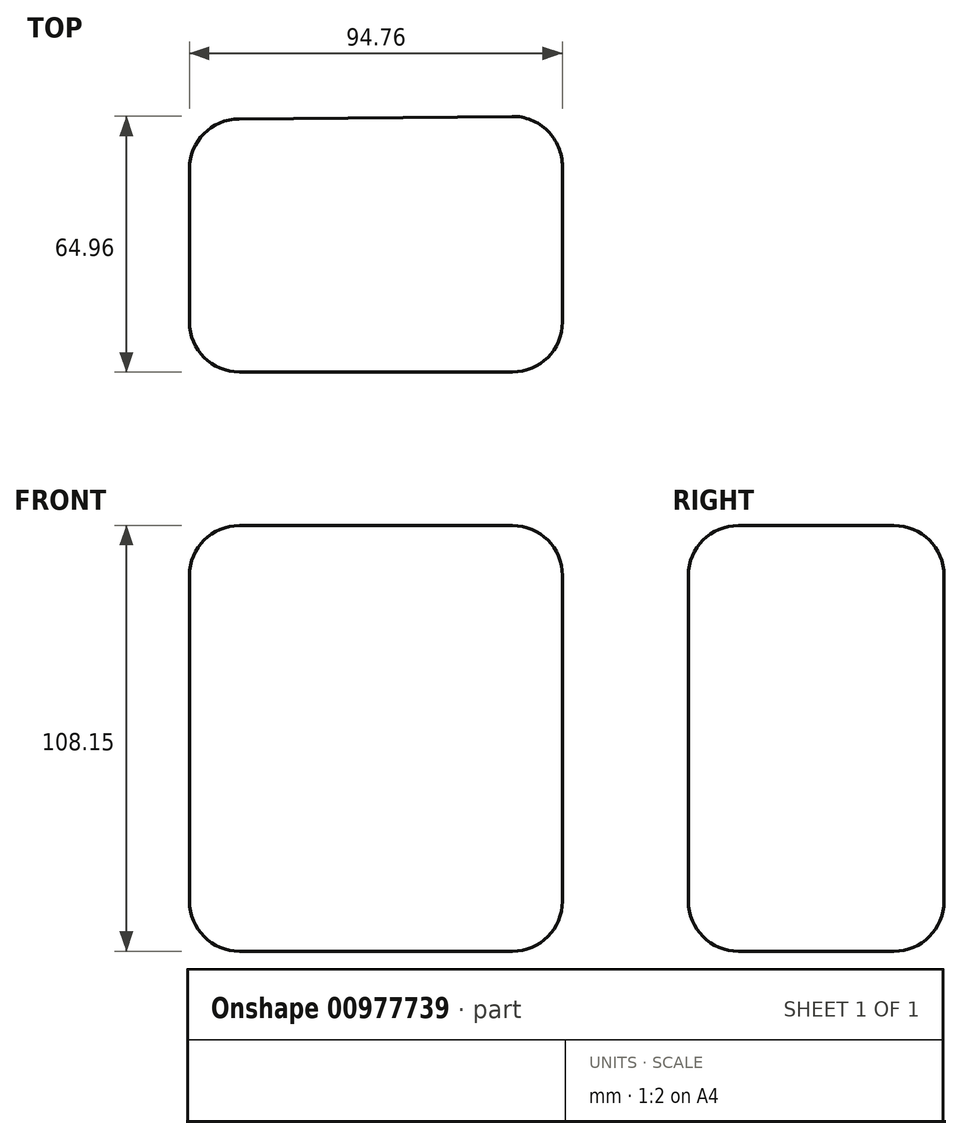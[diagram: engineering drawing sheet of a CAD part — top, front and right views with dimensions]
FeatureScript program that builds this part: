
annotation { "Feature Type Name" : "Feature", "Feature Type Description" : "" }
export const myFeature = defineFeature(function(context is Context, id is Id, definition is map)
    precondition{}
    {
        {
            var Q0;
            Q0=qCreatedBy(makeId("Top.planeOp"),FACE);
            var sketch = newSketch(context, id + "F0", { "sketchPlane" : qUnion([Q0])});
            skLineSegment(sketch, "E0", {"start": v(-60.1, 64.2) * mm, "end": v(-60.1, 0) * mm});
            skLineSegment(sketch, "E1", {"start": v(-60.1, 0) * mm, "end": v(0, 0) * mm});
            skLineSegment(sketch, "E2", {"start": v(0, 0) * mm, "end": v(34.66, 0) * mm});
            skLineSegment(sketch, "E3", {"start": v(34.66, 0) * mm, "end": v(34.66, 65.07) * mm});
            skLineSegment(sketch, "E4", {"start": v(34.66, 65.07) * mm, "end": v(-60.1, 64.2) * mm});
            skSolve(sketch);
        }
        {
            var Q0;
            Q0=makeQuery(id+"F0.imprint","IMPRINT",FACE,{"disambiguationData":[TD([[makeQuery(id+"F0.imprint","IMPRINT",EDGE,{"derivedFrom":sQuery(id+"F0.wireOp",EDGE,"E0")}),1.0]])]});
            extrude(context, id + "F1", {"entities" : qUnion([Q0]), "depth" : 108.15 * mm, "offsetDistance" : 25.4 * mm});
        }
        {
            var Q0;
            Q0=makeQuery(id+"F1.opExtrude","CAP_EDGE",EDGE,{"disambiguationData":[OSD([sQuery(id+"F0.wireOp",EDGE,"E0")])],"isStart":false});
            var Q1;
            Q1=makeQuery(id+"F1.opExtrude","CAP_EDGE",EDGE,{"disambiguationData":[OSD([sQuery(id+"F0.wireOp",EDGE,"E3")])],"isStart":false});
            var Q2;
            Q2=makeQuery(id+"F1.opExtrude","CAP_EDGE",EDGE,{"disambiguationData":[OSD([sQuery(id+"F0.wireOp",EDGE,"E0")])],"isStart":true});
            var Q3;
            Q3=makeQuery(id+"F1.opExtrude","CAP_FACE",FACE,{"disambiguationData":[OSD([sQuery(id+"F0.wireOp",EDGE,"E0"),sQuery(id+"F0.wireOp",EDGE,"E1"),sQuery(id+"F0.wireOp",EDGE,"E2"),sQuery(id+"F0.wireOp",EDGE,"E3"),sQuery(id+"F0.wireOp",EDGE,"E4")])],"isStart":true});
            var Q4;
            Q4=makeQuery(id+"F1.opExtrude","CAP_EDGE",EDGE,{"disambiguationData":[OSD([sQuery(id+"F0.wireOp",EDGE,"E1"),sQuery(id+"F0.wireOp",EDGE,"E2")])],"isStart":false});
            var Q5;
            Q5=makeQuery(id+"F1.opExtrude","SWEPT_EDGE",EDGE,{"disambiguationData":[OSD([sQuery(id+"F0.wireOp",EDGE,"E0"),sQuery(id+"F0.wireOp",EDGE,"E4")])]});
            var Q6;
            Q6=makeQuery(id+"F1.opExtrude","SWEPT_EDGE",EDGE,{"disambiguationData":[OSD([sQuery(id+"F0.wireOp",EDGE,"E2"),sQuery(id+"F0.wireOp",EDGE,"E3")])]});
            var Q7;
            Q7=makeQuery(id+"F1.opExtrude","SWEPT_EDGE",EDGE,{"disambiguationData":[OSD([sQuery(id+"F0.wireOp",EDGE,"E3"),sQuery(id+"F0.wireOp",EDGE,"E4")])]});
            var Q8;
            Q8=makeQuery(id+"F1.opExtrude","SWEPT_EDGE",EDGE,{"disambiguationData":[OSD([sQuery(id+"F0.wireOp",EDGE,"E0"),sQuery(id+"F0.wireOp",EDGE,"E1")])]});
            var Q9;
            Q9=makeQuery(id+"F1.opExtrude","CAP_EDGE",EDGE,{"disambiguationData":[OSD([sQuery(id+"F0.wireOp",EDGE,"E4")])],"isStart":false});
            fillet(context, id + "F2", {"entities" : qUnion([Q0, Q1, Q2, Q3, Q4, Q5, Q6, Q7, Q8, Q9]), "radius" : 12.7 * mm, "tangentPropagation" : true, "allowEdgeOverflow" : false});
        }
    });
